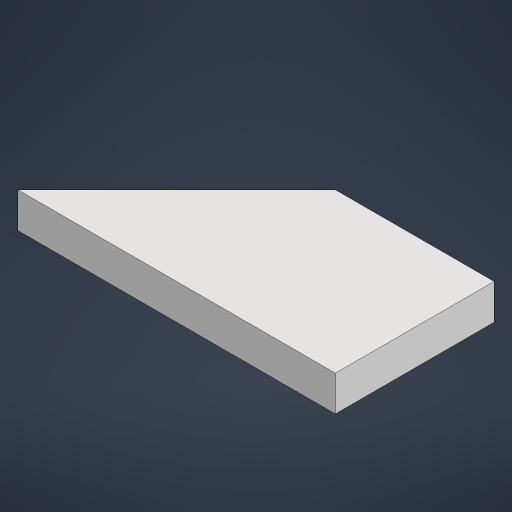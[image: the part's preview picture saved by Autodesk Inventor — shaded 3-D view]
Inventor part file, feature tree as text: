
AUTODESK INVENTOR PART (.ipt)
format: ipt  version: 2023.2 (Build 272271000, 271)  size: 153,088 bytes
history: native  units: in
note: dims shown in document units (in); Inventor stores cm internally (conversion verified against a paired STEP export)
features: extrude x1, sketch x1
ambient origin geometry x8: Origin, YZ Plane, XZ Plane, XY Plane, X Axis, Y Axis, Z Axis, Center Point
bodies: Solid1 (feature_tree)
feature tree (2):
  extrude  "Extrusion1"  Depth=18.0in
  sketch  "Sketch2"  dims[d3=36.0in d4=18.0in d5=135.0deg d6=4.0in d7=0.0in]
